# Revit family: Lighting_Fixture-Wall-Astro-7050_Leoxxxx
name_source: partatom
category: Lighting Fixtures
revit_build: Autodesk Revit LT 2014 (Build: 20130308_1515(x64)
units: mm (PartAtom-declared; Revit-internal decimal feet)

## types (4) — shared parameters
Apparent Load = 3 VA
Assembly Code = D5020200
Class = 1
Color Filter = 16777215
Description = Wall Light
Dimmable = No
Dimming Lamp Color Temperature Shift = <None>
Height = 120 mm  [stored 0.393701 ft]
IP Rating = IP20
Lamp = LED
Lamp included = Yes
Length = 340.2 mm  [stored 1.11614 ft]
Light Source Elevation = 1000 mm  [stored 3.28084 ft]
Light Source From Wall = 1500 mm  [stored 4.92126 ft]
Luminaire Lamp Efficiency Rating = A
Manufacturer = Astro Lighting Ltd, CM20 2DP
Mountable on normally flammable surfaces = Yes
Number of Poles = 1
Photometric Web File = 7050 LEO SWITCHED CHROME 25-07-2013.ies
Product Documentation = http://www.astrolighting.co.uk
Suitable for bathroom zone = Zone 3
Tilt Angle = 90.00°
Type Comments = Includes integral LED driver. Includes integral switch. Cut out: 107mm high x 30mm wide x 55mm depth.
URL = www.astrolighting.co.uk
Voltage = 230 V
Wattage Comments = 3w
Weight = 1.2kg
Width = 45 mm  [stored 0.147638 ft]

## per-type parameters (varying)
| type | Arm Material | Casing Material | Model |
| 7050 Leo (Chrome) | Astro - Steel - Chrome Finish | Astro - Steel - Chrome Finish | 7050 Leo Switched Chrome |
| 7052 Leo (Bronze) | Astro - Steel - Bronze | Astro - Steel - Bronze | 7050 Leo Switched Bronze |
| 7167 Leo (White) | Astro - Steel - Chrome Finish | Astro - Steel - White | 7050 Leo Switched White |
| 7051 Leo (Matt Nickel) | Astro - Steel - Matt Nickel | Astro - Steel - Matt Nickel | 7050 Leo Switched Matt Nickel |

note: [stored X ft] marks values corroborated as IEEE doubles in the binary element streams (Revit-internal decimal feet)

## geometry (parser evidence)
native form markers: Sweep x1
no freeform markers — native parametric forms only
